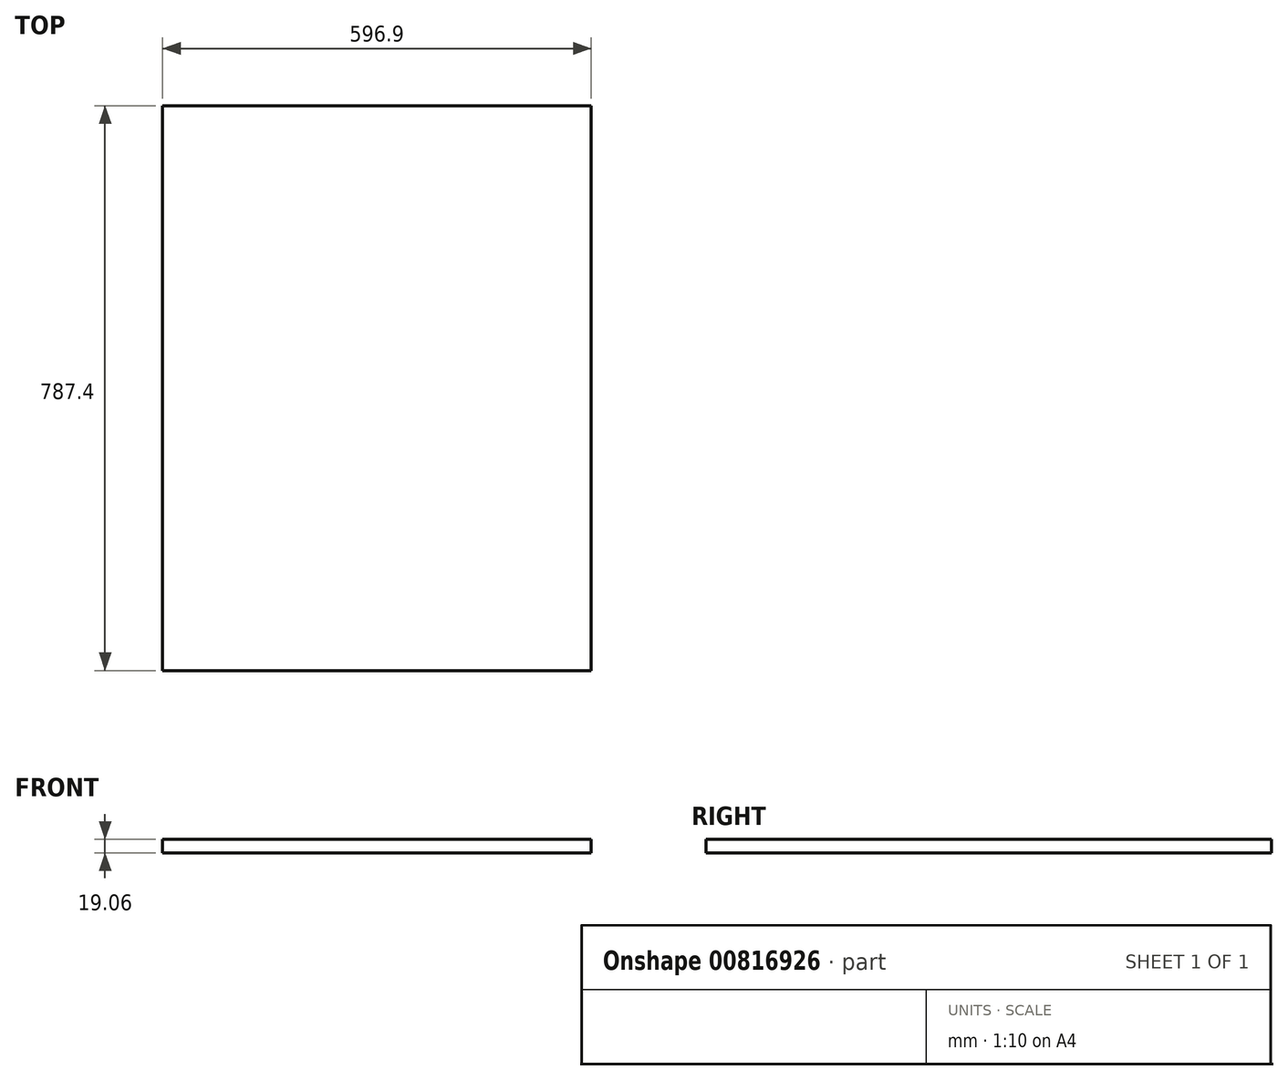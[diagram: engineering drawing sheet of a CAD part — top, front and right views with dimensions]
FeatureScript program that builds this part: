
annotation { "Feature Type Name" : "Feature", "Feature Type Description" : "" }
export const myFeature = defineFeature(function(context is Context, id is Id, definition is map)
    precondition{}
    {
        {
            var Q0;
            Q0=qCreatedBy(makeId("Top.planeOp"),FACE);
            var sketch = newSketch(context, id + "F0", { "sketchPlane" : qUnion([Q0])});
            skLineSegment(sketch, "E0.bottom", {"start": v(-298.45, -393.7) * mm, "end": v(298.45, -393.7) * mm});
            skLineSegment(sketch, "E0.top", {"start": v(-298.45, 393.7) * mm, "end": v(298.45, 393.7) * mm});
            skLineSegment(sketch, "E0.left", {"start": v(-298.45, -393.7) * mm, "end": v(-298.45, 393.7) * mm});
            skLineSegment(sketch, "E0.right", {"start": v(298.45, -393.7) * mm, "end": v(298.45, 393.7) * mm});
            skPoint(sketch, "E1", {"position": v(-298.45, 0) * mm});
            skPoint(sketch, "E2", {"position": v(0, 393.7) * mm});
            skSolve(sketch);
        }
        {
            var Q0;
            Q0=makeQuery(id+"F0.imprint","IMPRINT",FACE,{"disambiguationData":[TD([[makeQuery(id+"F0.imprint","IMPRINT",EDGE,{"derivedFrom":sQuery(id+"F0.wireOp",EDGE,"E0.bottom")}),1.0]])]});
            extrude(context, id + "F1", {"entities" : qUnion([Q0]), "endBound" : BoundingType.SYMMETRIC, "depth" : 19.05 * mm, "offsetDistance" : 25.4 * mm});
        }
    });
